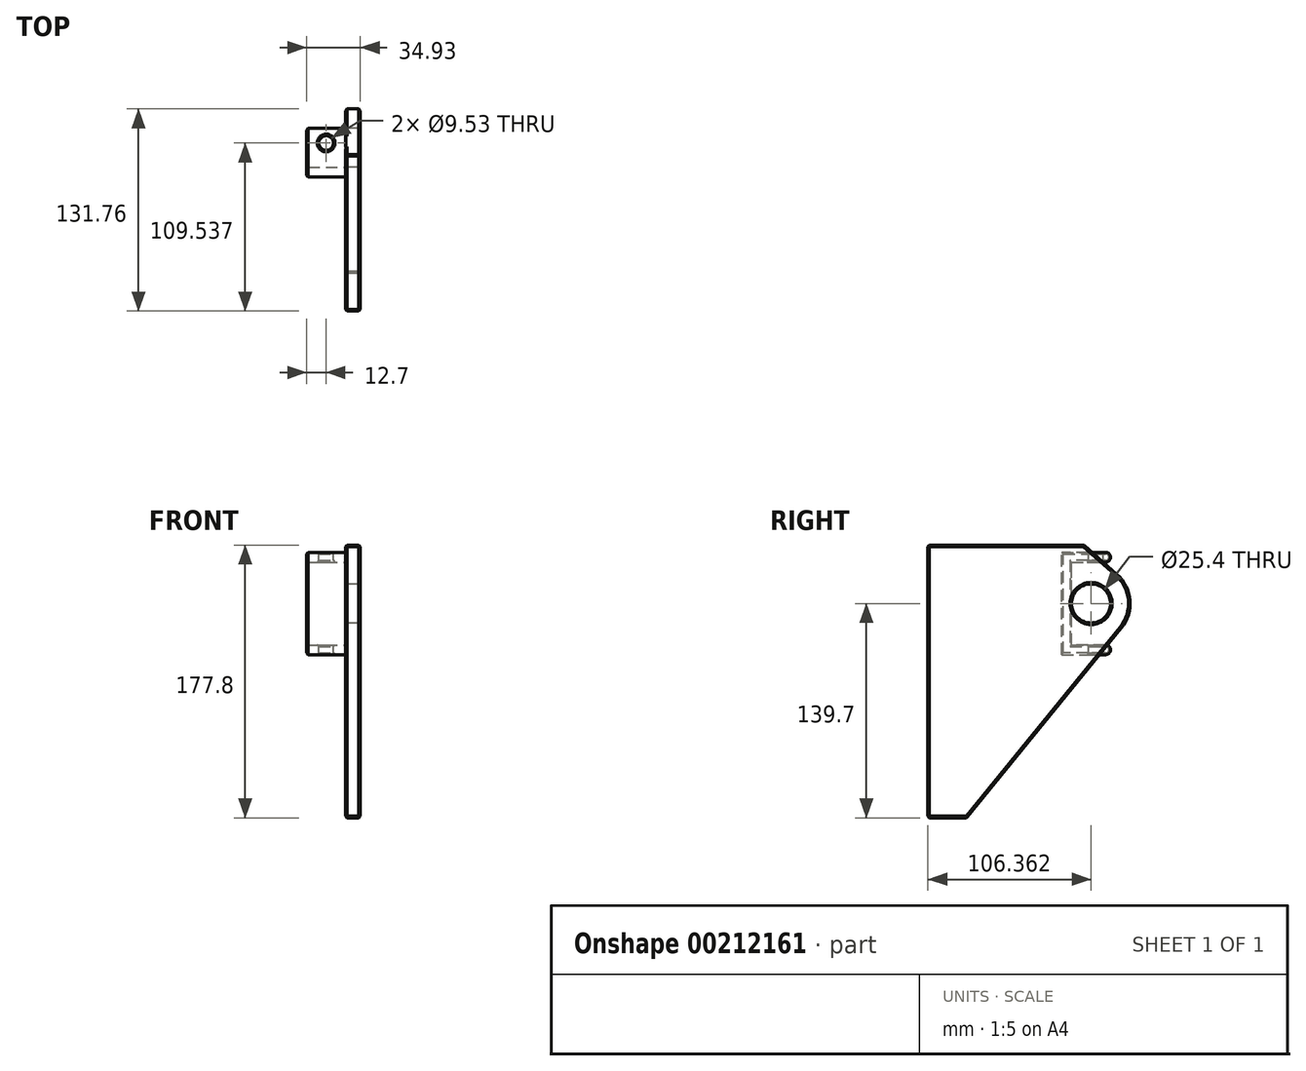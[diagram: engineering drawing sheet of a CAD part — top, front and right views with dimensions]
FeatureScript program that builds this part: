
annotation { "Feature Type Name" : "Feature", "Feature Type Description" : "" }
export const myFeature = defineFeature(function(context is Context, id is Id, definition is map)
    precondition{}
    {
        {
            var Q0;
            Q0=qCreatedBy(makeId("Right.planeOp"),FACE);
            var sketch = newSketch(context, id + "F0", { "sketchPlane" : qUnion([Q0])});
            skLineSegment(sketch, "E0", {"start": v(0, 0) * mm, "end": v(0, 177.8) * mm});
            skLineSegment(sketch, "E1", {"start": v(0, 177.8) * mm, "end": v(101.6, 177.8) * mm});
            skLineSegment(sketch, "E2", {"start": v(25.4, 0) * mm, "end": v(0, 0) * mm});
            skCircle(sketch, "E3", {"center": v(106.36, 139.7) * mm, "radius": 12.7 * mm});
            skLineSegment(sketch, "E4", {"start": v(25.4, 0) * mm, "end": v(126.06, 123.67) * mm});
            skLineSegment(sketch, "E5", {"start": v(101.6, 177.8) * mm, "end": v(123.18, 158.74) * mm});
            skArc(sketch, "E6", {"start": v(126.06, 123.67) * mm, "mid": v(131.68, 141.78) * mm, "end": v(123.18, 158.74) * mm});
            skSolve(sketch);
        }
        {
            var Q0;
            Q0=makeQuery(id+"F0.imprint","IMPRINT",FACE,{"disambiguationData":[TD([[makeQuery(id+"F0.imprint","IMPRINT",EDGE,{"derivedFrom":sQuery(id+"F0.wireOp",EDGE,"E0")}),-1.0]])]});
            extrude(context, id + "F1", {"entities" : qUnion([Q0]), "depth" : 9.52 * mm});
        }
        {
            var Q0;
            Q0=makeQuery(id+"F1.opExtrude","CAP_FACE",FACE,{"disambiguationData":[OSD([sQuery(id+"F0.wireOp",EDGE,"E0"),sQuery(id+"F0.wireOp",EDGE,"E1"),sQuery(id+"F0.wireOp",EDGE,"E2"),sQuery(id+"F0.wireOp",EDGE,"E3"),sQuery(id+"F0.wireOp",EDGE,"E4"),sQuery(id+"F0.wireOp",EDGE,"E5"),sQuery(id+"F0.wireOp",EDGE,"E6")])],"isStart":true});
            var sketch = newSketch(context, id + "F2", { "sketchPlane" : qUnion([Q0])});
            skLineSegment(sketch, "E7", {"start": v(-106.36, 139.7) * mm, "end": v(133.79, 139.7) * mm, "construction": true});
            skLineSegment(sketch, "E8", {"start": v(-106.36, 139.7) * mm, "end": v(-106.36, -37.97) * mm, "construction": true});
            skLineSegment(sketch, "E9", {"start": v(-106.36, 139.7) * mm, "end": v(-106.36, 193.68) * mm, "construction": true});
            skLineSegment(sketch, "E10", {"start": v(-131.76, 109.54) * mm, "end": v(-131.76, 109.54) * mm});
            skLineSegment(sketch, "E11", {"start": v(-135.09, 169.86) * mm, "end": v(-135.09, 169.86) * mm});
            skPoint(sketch, "E12.visualSharp", {"position": v(-135.09, 173.04) * mm});
            skPoint(sketch, "E13.visualSharp", {"position": v(-135.09, 166.69) * mm});
            skPoint(sketch, "E14.visualSharp", {"position": v(-131.76, 112.71) * mm});
            skPoint(sketch, "E15.visualSharp", {"position": v(-131.76, 106.36) * mm});
            skLineSegment(sketch, "E16", {"start": v(-93.66, 139.7) * mm, "end": v(-93.66, 166.69) * mm});
            skLineSegment(sketch, "E17", {"start": v(-93.66, 139.7) * mm, "end": v(-93.66, 112.71) * mm});
            skLineSegment(sketch, "E18.0", {"start": v(-87.31, 139.7) * mm, "end": v(-87.31, 173.04) * mm});
            skLineSegment(sketch, "E19.0", {"start": v(-87.31, 139.7) * mm, "end": v(-87.31, 106.36) * mm});
            skLineSegment(sketch, "E20", {"start": v(-87.31, 173.04) * mm, "end": v(-115.89, 173.04) * mm});
            skLineSegment(sketch, "E21.0", {"start": v(-93.66, 166.69) * mm, "end": v(-115.89, 166.69) * mm});
            skLineSegment(sketch, "E22", {"start": v(-87.31, 106.36) * mm, "end": v(-115.89, 106.36) * mm});
            skLineSegment(sketch, "E23.0", {"start": v(-93.66, 112.71) * mm, "end": v(-115.89, 112.71) * mm});
            skLineSegment(sketch, "E24", {"start": v(-119.06, 169.86) * mm, "end": v(-119.06, 169.86) * mm});
            skLineSegment(sketch, "E25", {"start": v(-119.06, 109.54) * mm, "end": v(-119.06, 109.54) * mm});
            skPoint(sketch, "E26.visualSharp", {"position": v(-119.06, 112.71) * mm});
            skArc(sketch, "E26.filletArc", {"start": v(-115.89, 112.71) * mm, "mid": v(-118.13, 111.78) * mm, "end": v(-119.06, 109.54) * mm});
            skPoint(sketch, "E27.visualSharp", {"position": v(-119.06, 106.36) * mm});
            skArc(sketch, "E27.filletArc", {"start": v(-119.06, 109.54) * mm, "mid": v(-118.13, 107.3) * mm, "end": v(-115.89, 106.36) * mm});
            skPoint(sketch, "E28.visualSharp", {"position": v(-119.06, 173.04) * mm});
            skArc(sketch, "E28.filletArc", {"start": v(-115.89, 173.04) * mm, "mid": v(-118.13, 172.1) * mm, "end": v(-119.06, 169.86) * mm});
            skPoint(sketch, "E29.visualSharp", {"position": v(-119.06, 166.69) * mm});
            skArc(sketch, "E29.filletArc", {"start": v(-119.06, 169.86) * mm, "mid": v(-118.13, 167.62) * mm, "end": v(-115.89, 166.69) * mm});
            skSolve(sketch);
        }
        {
            var Q0;
            {var subQ6=sQuery(id+"F2.wireOp",EDGE,"E16");Q0=makeQuery(id+"F2.imprint","IMPRINT",FACE,{"disambiguationData":[TD([[makeQuery(id+"F2.imprint","IMPRINT",EDGE,{"derivedFrom":subQ6}),-1.0]])]});}
            var Q1;
            {var subQ1=sQuery(id+"F2.wireOp",EDGE,"E28.filletArc");Q1=makeQuery(id+"F2.imprint","IMPRINT",FACE,{"disambiguationData":[TD([[makeQuery(id+"F2.imprint","IMPRINT",EDGE,{"derivedFrom":subQ1}),1.0]])]});}
            var Q2;
            {var subQ0=sQuery(id+"F2.wireOp",EDGE,"E27.filletArc");Q2=makeQuery(id+"F2.imprint","IMPRINT",FACE,{"disambiguationData":[TD([[makeQuery(id+"F2.imprint","IMPRINT",EDGE,{"derivedFrom":subQ0}),1.0]])]});}
            extrude(context, id + "F3", {"entities" : qUnion([Q0, Q1, Q2]), "operationType" : NewBodyOperationType.ADD, "depth" : 25.4 * mm});
        }
        {
            var Q0;
            Q0=makeQuery(id+"F3.opExtrude","SWEPT_FACE",FACE,{"disambiguationData":[OSD([sQuery(id+"F2.wireOp",EDGE,"E20")])]});
            var sketch = newSketch(context, id + "F4", { "sketchPlane" : qUnion([Q0])});
            skCircle(sketch, "E30", {"center": v(-12.7, 109.54) * mm, "radius": 4.76 * mm});
            skSolve(sketch);
        }
        {
            var Q0;
            Q0=makeQuery(id+"F4.imprint","IMPRINT",FACE,{"disambiguationData":[TD([[makeQuery(id+"F4.imprint","IMPRINT",EDGE,{"derivedFrom":sQuery(id+"F4.wireOp",EDGE,"E30")}),1.0]])]});
            extrude(context, id + "F5", {"entities" : qUnion([Q0]), "operationType" : NewBodyOperationType.REMOVE, "endBound" : BoundingType.THROUGH_ALL, "oppositeDirection" : true, "depth" : 25.4 * mm});
        }
        {
            var Q0;
            Q0=makeQuery(id+"F1.opExtrude","CAP_FACE",FACE,{"disambiguationData":[OSD([sQuery(id+"F0.wireOp",EDGE,"E0"),sQuery(id+"F0.wireOp",EDGE,"E1"),sQuery(id+"F0.wireOp",EDGE,"E2"),sQuery(id+"F0.wireOp",EDGE,"E3"),sQuery(id+"F0.wireOp",EDGE,"E4"),sQuery(id+"F0.wireOp",EDGE,"E5"),sQuery(id+"F0.wireOp",EDGE,"E6")])],"isStart":false});
            var Q1;
            Q1=makeQuery(id+"F1.opExtrude","SWEPT_FACE",FACE,{"disambiguationData":[OSD([sQuery(id+"F0.wireOp",EDGE,"E0")])]});
            var Q2;
            Q2=makeQuery(id+"F1.opExtrude","SWEPT_FACE",FACE,{"disambiguationData":[OSD([sQuery(id+"F0.wireOp",EDGE,"E1")])]});
            var Q3;
            {var subQ0=sQuery(id+"F0.wireOp",EDGE,"E5");var subQ1=sQuery(id+"F0.wireOp",EDGE,"E1");var subQ2=sQuery(id+"F2.wireOp",EDGE,"E20");Q3=makeQuery(id+"F3.boolean.opBoolean","SPLIT",EDGE,{"disambiguationData":[TD([makeQuery(id+"F1.opExtrude","CAP_FACE",FACE,{"disambiguationData":[OSD([sQuery(id+"F0.wireOp",EDGE,"E0"),subQ1,sQuery(id+"F0.wireOp",EDGE,"E2"),sQuery(id+"F0.wireOp",EDGE,"E3"),sQuery(id+"F0.wireOp",EDGE,"E4"),subQ0,sQuery(id+"F0.wireOp",EDGE,"E6")])],"isStart":true}),makeQuery(id+"F1.opExtrude","SWEPT_FACE",FACE,{"disambiguationData":[OSD([subQ1])]}),makeQuery(id+"F1.opExtrude","SWEPT_FACE",FACE,{"disambiguationData":[OSD([subQ0])]}),makeQuery(id+"F3.opExtrude","CAP_FACE",FACE,{"disambiguationData":[OSD([sQuery(id+"F2.wireOp",EDGE,"E16"),sQuery(id+"F2.wireOp",EDGE,"E17"),sQuery(id+"F2.wireOp",EDGE,"E18.0"),sQuery(id+"F2.wireOp",EDGE,"E19.0"),subQ2,sQuery(id+"F2.wireOp",EDGE,"E21.0"),sQuery(id+"F2.wireOp",EDGE,"E22"),sQuery(id+"F2.wireOp",EDGE,"E23.0"),sQuery(id+"F2.wireOp",EDGE,"E26.filletArc"),sQuery(id+"F2.wireOp",EDGE,"E27.filletArc"),sQuery(id+"F2.wireOp",EDGE,"E28.filletArc"),sQuery(id+"F2.wireOp",EDGE,"E29.filletArc")])],"isStart":true}),makeQuery(id+"F3.opExtrude","SWEPT_FACE",FACE,{"disambiguationData":[OSD([subQ2])]})])],"derivedFrom":makeQuery(id+"F1.opExtrude","CAP_EDGE",EDGE,{"disambiguationData":[OSD([subQ0])],"isStart":true})});}
            var Q4;
            {var subQ0=sQuery(id+"F0.wireOp",EDGE,"E6");var subQ1=sQuery(id+"F0.wireOp",EDGE,"E5");var subQ2=sQuery(id+"F2.wireOp",EDGE,"E21.0");Q4=makeQuery(id+"F3.boolean.opBoolean","SPLIT",EDGE,{"disambiguationData":[TD([makeQuery(id+"F1.opExtrude","CAP_FACE",FACE,{"disambiguationData":[OSD([sQuery(id+"F0.wireOp",EDGE,"E0"),sQuery(id+"F0.wireOp",EDGE,"E1"),sQuery(id+"F0.wireOp",EDGE,"E2"),sQuery(id+"F0.wireOp",EDGE,"E3"),sQuery(id+"F0.wireOp",EDGE,"E4"),subQ1,subQ0])],"isStart":true}),makeQuery(id+"F1.opExtrude","SWEPT_FACE",FACE,{"disambiguationData":[OSD([subQ1])]}),makeQuery(id+"F1.opExtrude","SWEPT_FACE",FACE,{"disambiguationData":[OSD([subQ0])]}),makeQuery(id+"F3.opExtrude","CAP_FACE",FACE,{"disambiguationData":[OSD([sQuery(id+"F2.wireOp",EDGE,"E16"),sQuery(id+"F2.wireOp",EDGE,"E17"),sQuery(id+"F2.wireOp",EDGE,"E18.0"),sQuery(id+"F2.wireOp",EDGE,"E19.0"),sQuery(id+"F2.wireOp",EDGE,"E20"),subQ2,sQuery(id+"F2.wireOp",EDGE,"E22"),sQuery(id+"F2.wireOp",EDGE,"E23.0"),sQuery(id+"F2.wireOp",EDGE,"E26.filletArc"),sQuery(id+"F2.wireOp",EDGE,"E27.filletArc"),sQuery(id+"F2.wireOp",EDGE,"E28.filletArc"),sQuery(id+"F2.wireOp",EDGE,"E29.filletArc")])],"isStart":true}),makeQuery(id+"F3.opExtrude","SWEPT_FACE",FACE,{"disambiguationData":[OSD([subQ2])]})])],"derivedFrom":makeQuery(id+"F1.opExtrude","CAP_EDGE",EDGE,{"disambiguationData":[OSD([subQ1])],"isStart":true})});}
            var Q5;
            {var subQ0=sQuery(id+"F0.wireOp",EDGE,"E4");var subQ1=sQuery(id+"F0.wireOp",EDGE,"E2");var subQ2=sQuery(id+"F2.wireOp",EDGE,"E22");Q5=makeQuery(id+"F3.boolean.opBoolean","SPLIT",EDGE,{"disambiguationData":[TD([makeQuery(id+"F1.opExtrude","CAP_FACE",FACE,{"disambiguationData":[OSD([sQuery(id+"F0.wireOp",EDGE,"E0"),sQuery(id+"F0.wireOp",EDGE,"E1"),subQ1,sQuery(id+"F0.wireOp",EDGE,"E3"),subQ0,sQuery(id+"F0.wireOp",EDGE,"E5"),sQuery(id+"F0.wireOp",EDGE,"E6")])],"isStart":true}),makeQuery(id+"F1.opExtrude","SWEPT_FACE",FACE,{"disambiguationData":[OSD([subQ1])]}),makeQuery(id+"F1.opExtrude","SWEPT_FACE",FACE,{"disambiguationData":[OSD([subQ0])]}),makeQuery(id+"F3.opExtrude","CAP_FACE",FACE,{"disambiguationData":[OSD([sQuery(id+"F2.wireOp",EDGE,"E16"),sQuery(id+"F2.wireOp",EDGE,"E17"),sQuery(id+"F2.wireOp",EDGE,"E18.0"),sQuery(id+"F2.wireOp",EDGE,"E19.0"),sQuery(id+"F2.wireOp",EDGE,"E20"),sQuery(id+"F2.wireOp",EDGE,"E21.0"),subQ2,sQuery(id+"F2.wireOp",EDGE,"E23.0"),sQuery(id+"F2.wireOp",EDGE,"E26.filletArc"),sQuery(id+"F2.wireOp",EDGE,"E27.filletArc"),sQuery(id+"F2.wireOp",EDGE,"E28.filletArc"),sQuery(id+"F2.wireOp",EDGE,"E29.filletArc")])],"isStart":true}),makeQuery(id+"F3.opExtrude","SWEPT_FACE",FACE,{"disambiguationData":[OSD([subQ2])]})])],"derivedFrom":makeQuery(id+"F1.opExtrude","CAP_EDGE",EDGE,{"disambiguationData":[OSD([subQ0])],"isStart":true})});}
            var Q6;
            Q6=makeQuery(id+"F1.opExtrude","SWEPT_EDGE",EDGE,{"disambiguationData":[OSD([sQuery(id+"F0.wireOp",EDGE,"E2"),sQuery(id+"F0.wireOp",EDGE,"E4")])]});
            var Q7;
            Q7=makeQuery(id+"F1.opExtrude","CAP_EDGE",EDGE,{"disambiguationData":[OSD([sQuery(id+"F0.wireOp",EDGE,"E2")])],"isStart":true});
            var Q8;
            Q8=makeQuery(id+"F3.opExtrude","CAP_FACE",FACE,{"disambiguationData":[OSD([sQuery(id+"F2.wireOp",EDGE,"E16"),sQuery(id+"F2.wireOp",EDGE,"E17"),sQuery(id+"F2.wireOp",EDGE,"E18.0"),sQuery(id+"F2.wireOp",EDGE,"E19.0"),sQuery(id+"F2.wireOp",EDGE,"E20"),sQuery(id+"F2.wireOp",EDGE,"E21.0"),sQuery(id+"F2.wireOp",EDGE,"E22"),sQuery(id+"F2.wireOp",EDGE,"E23.0"),sQuery(id+"F2.wireOp",EDGE,"E26.filletArc"),sQuery(id+"F2.wireOp",EDGE,"E27.filletArc"),sQuery(id+"F2.wireOp",EDGE,"E28.filletArc"),sQuery(id+"F2.wireOp",EDGE,"E29.filletArc")])],"isStart":false});
            var Q9;
            Q9=makeQuery(id+"F1.opExtrude","CAP_EDGE",EDGE,{"disambiguationData":[OSD([sQuery(id+"F0.wireOp",EDGE,"E3")])],"isStart":true});
            var Q10;
            Q10=makeQuery(id+"F5.boolean.opBoolean","COPY",FACE,{"disambiguationData":[TD([makeQuery(id+"F3.opExtrude","SWEPT_FACE",FACE,{"disambiguationData":[OSD([sQuery(id+"F2.wireOp",EDGE,"E22")])]})])],"derivedFrom":makeQuery(id+"F5.opExtrude","SWEPT_FACE",FACE,{"disambiguationData":[OSD([sQuery(id+"F4.wireOp",EDGE,"E30")])]})});
            var Q11;
            Q11=makeQuery(id+"F5.boolean.opBoolean","COPY",FACE,{"disambiguationData":[TD([makeQuery(id+"F3.opExtrude","SWEPT_FACE",FACE,{"disambiguationData":[OSD([sQuery(id+"F2.wireOp",EDGE,"E20")])]})])],"derivedFrom":makeQuery(id+"F5.opExtrude","SWEPT_FACE",FACE,{"disambiguationData":[OSD([sQuery(id+"F4.wireOp",EDGE,"E30")])]})});
            chamfer(context, id + "F6", {"entities" : qUnion([Q0, Q1, Q2, Q3, Q4, Q5, Q6, Q7, Q8, Q9, Q10, Q11]), "width" : 1.02 * mm, "tangentPropagation" : true});
        }
    });
